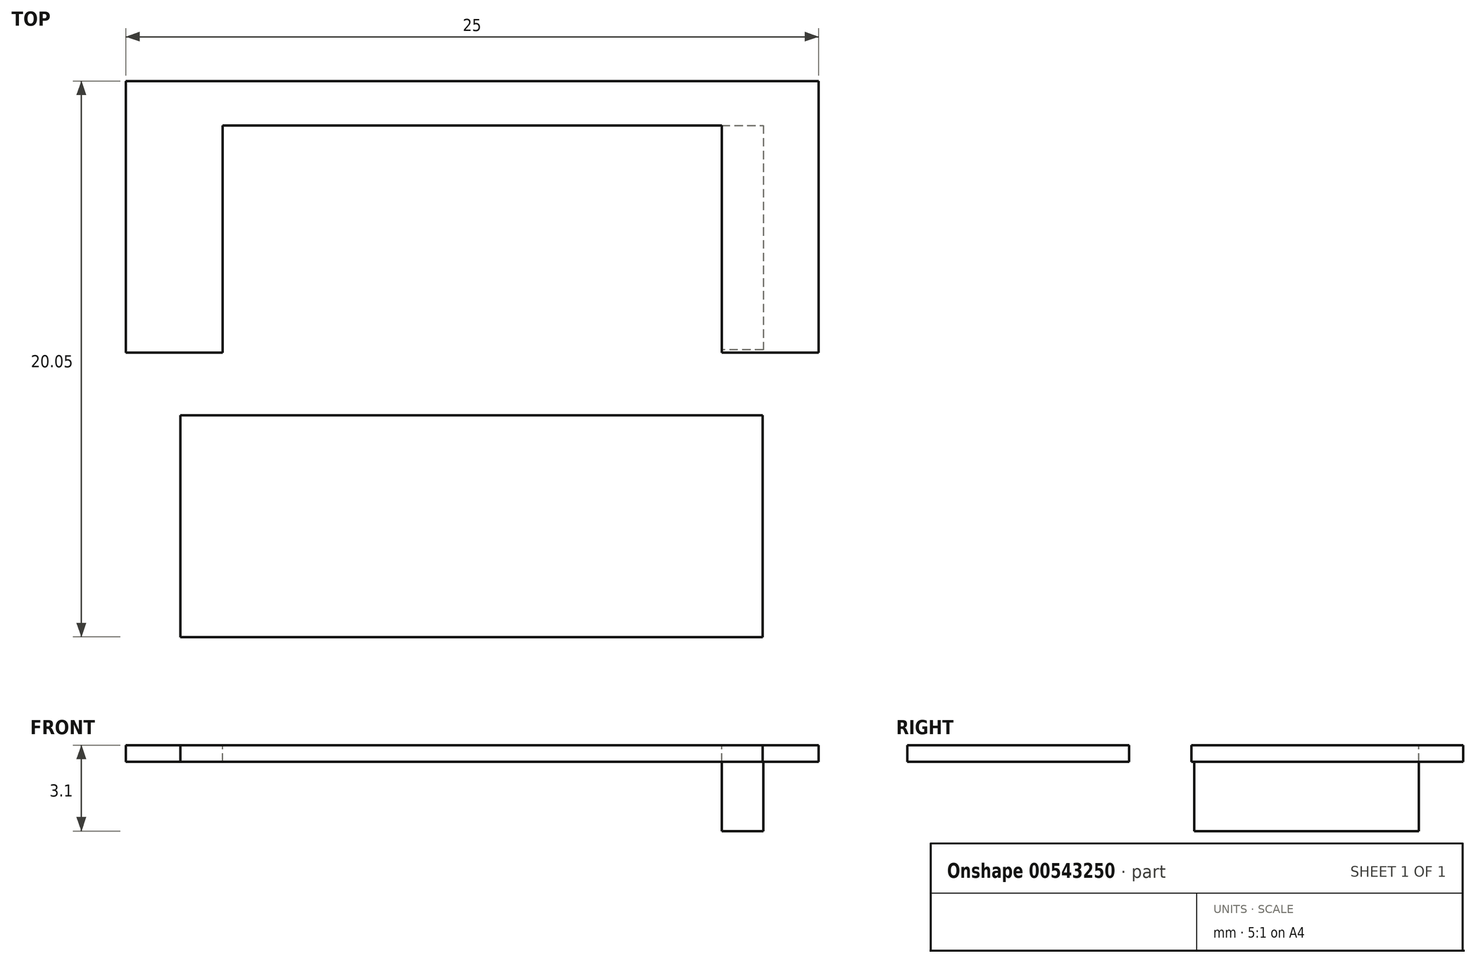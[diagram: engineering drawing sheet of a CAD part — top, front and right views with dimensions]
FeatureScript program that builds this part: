
annotation { "Feature Type Name" : "Feature", "Feature Type Description" : "" }
export const myFeature = defineFeature(function(context is Context, id is Id, definition is map)
    precondition{}
    {
        {
            var Q0;
            Q0=qCreatedBy(makeId("Top.planeOp"),FACE);
            var sketch = newSketch(context, id + "F0", { "sketchPlane" : qUnion([Q0])});
            skLineSegment(sketch, "E0.bottom", {"start": v(-20.52, -0.28) * mm, "end": v(4.48, -0.28) * mm});
            skLineSegment(sketch, "E0.top", {"start": v(-20.52, -10.08) * mm, "end": v(4.48, -10.08) * mm});
            skLineSegment(sketch, "E0.left", {"start": v(-20.52, -0.28) * mm, "end": v(-20.52, -10.08) * mm});
            skLineSegment(sketch, "E0.right", {"start": v(4.48, -0.28) * mm, "end": v(4.48, -10.08) * mm});
            skLineSegment(sketch, "E1.bottom", {"start": v(-17.02, -3.48) * mm, "end": v(0.98, -3.48) * mm});
            skLineSegment(sketch, "E1.top", {"start": v(-17.02, -6.98) * mm, "end": v(0.98, -6.98) * mm});
            skLineSegment(sketch, "E1.left", {"start": v(-17.02, -3.48) * mm, "end": v(-17.02, -6.98) * mm});
            skLineSegment(sketch, "E1.right", {"start": v(0.98, -3.48) * mm, "end": v(0.98, -6.98) * mm});
            skLineSegment(sketch, "E2", {"start": v(-17.02, -6.98) * mm, "end": v(-17.02, -10.08) * mm});
            skLineSegment(sketch, "E3", {"start": v(0.98, -6.98) * mm, "end": v(0.98, -10.08) * mm});
            skLineSegment(sketch, "E4", {"start": v(-17.02, -3.48) * mm, "end": v(-17.02, -0.28) * mm});
            skLineSegment(sketch, "E5", {"start": v(0.98, -3.48) * mm, "end": v(0.98, -0.28) * mm});
            skLineSegment(sketch, "E6", {"start": v(-17.02, -10.08) * mm, "end": v(-18.52, -10.08) * mm});
            skLineSegment(sketch, "E7", {"start": v(-18.52, -10.08) * mm, "end": v(-18.52, -1.88) * mm});
            skLineSegment(sketch, "E8", {"start": v(-18.52, -1.88) * mm, "end": v(2.48, -1.88) * mm});
            skLineSegment(sketch, "E9", {"start": v(2.48, -1.88) * mm, "end": v(2.48, -9.98) * mm});
            skLineSegment(sketch, "E10", {"start": v(2.48, -9.98) * mm, "end": v(0.98, -9.98) * mm});
            skLineSegment(sketch, "E11.bottom", {"start": v(-18.54, -12.33) * mm, "end": v(2.46, -12.33) * mm});
            skLineSegment(sketch, "E11.top", {"start": v(-18.54, -20.33) * mm, "end": v(2.46, -20.33) * mm});
            skLineSegment(sketch, "E11.left", {"start": v(-18.54, -12.33) * mm, "end": v(-18.54, -20.33) * mm});
            skLineSegment(sketch, "E11.right", {"start": v(2.46, -12.33) * mm, "end": v(2.46, -20.33) * mm});
            skCircle(sketch, "E12", {"center": v(-8.02, -5.58) * mm, "radius": 2.85 * mm});
            skPoint(sketch, "E12.centerSnap0", {"position": v(-8.02, -3.48) * mm});
            skSolve(sketch);
        }
        {
            var Q0;
            Q0 = qSketchRegion(id + "F0", true);
            var Q1;
            {var subQ7=sQuery(id+"F0.wireOp",EDGE,"E6");Q1=makeQuery(id+"F0.imprint","IMPRINT",FACE,{"disambiguationData":[TD([[makeQuery(id+"F0.imprint","IMPRINT",EDGE,{"derivedFrom":subQ7}),-1.0]])]});}
            var Q2;
            {var subQ8=sQuery(id+"F0.wireOp",EDGE,"E9");Q2=makeQuery(id+"F0.imprint","IMPRINT",FACE,{"disambiguationData":[TD([[makeQuery(id+"F0.imprint","IMPRINT",EDGE,{"derivedFrom":subQ8}),-1.0]])]});}
            var Q3;
            {var subQ0=sQuery(id+"F0.wireOp",EDGE,"E1.bottom");Q3=makeQuery(id+"F0.imprint","IMPRINT",FACE,{"disambiguationData":[TD([[makeQuery(id+"F0.imprint","IMPRINT",EDGE,{"derivedFrom":subQ0}),1.0]])]});}
            extrude(context, id + "F1", {"entities" : qUnion([Q0, Q1, Q2, Q3]), "depth" : 0.6 * mm, "offsetDistance" : 25 * mm});
        }
        {
            var Q0;
            Q0=makeQuery(id+"F0.imprint","IMPRINT",FACE,{"disambiguationData":[TD([[makeQuery(id+"F0.imprint","IMPRINT",EDGE,{"derivedFrom":sQuery(id+"F0.wireOp",EDGE,"E1.top")}),-1.0]])]});
            extrude(context, id + "F2", {"entities" : qUnion([Q0]), "operationType" : NewBodyOperationType.ADD, "oppositeDirection" : true, "depth" : 4 * mm, "offsetDistance" : 25 * mm});
        }
        {
            var Q0;
            Q0=makeQuery(id+"F2.opExtrude","CAP_EDGE",EDGE,{"disambiguationData":[OSD([sQuery(id+"F0.wireOp",EDGE,"E1.top")])],"isStart":false});
            var Q1;
            Q1=makeQuery(id+"F2.opExtrude","CAP_EDGE",EDGE,{"disambiguationData":[OSD([sQuery(id+"F0.wireOp",EDGE,"E12")])],"isStart":false});
            chamfer(context, id + "F3", {"entities" : qUnion([Q0, Q1]), "width" : 4.6 * mm, "tangentPropagation" : true});
        }
        {
            var Q0;
            Q0=makeQuery(id+"F1.opExtrude","CAP_EDGE",EDGE,{"disambiguationData":[OSD([sQuery(id+"F0.wireOp",EDGE,"E1.bottom")])],"isStart":false});
            chamfer(context, id + "F4", {"entities" : qUnion([Q0]), "width" : 0.6 * mm, "tangentPropagation" : true});
        }
        {
            var Q0;
            {var subQ7=sQuery(id+"F0.wireOp",EDGE,"E6");Q0=makeQuery(id+"F0.imprint","IMPRINT",FACE,{"disambiguationData":[TD([[makeQuery(id+"F0.imprint","IMPRINT",EDGE,{"derivedFrom":subQ7}),-1.0]])]});}
            var Q1;
            {var subQ0=sQuery(id+"F0.wireOp",EDGE,"E1.bottom");Q1=makeQuery(id+"F0.imprint","IMPRINT",FACE,{"disambiguationData":[TD([[makeQuery(id+"F0.imprint","IMPRINT",EDGE,{"derivedFrom":subQ0}),1.0]])]});}
            var Q2;
            {var subQ8=sQuery(id+"F0.wireOp",EDGE,"E9");Q2=makeQuery(id+"F0.imprint","IMPRINT",FACE,{"disambiguationData":[TD([[makeQuery(id+"F0.imprint","IMPRINT",EDGE,{"derivedFrom":subQ8}),-1.0]])]});}
            extrude(context, id + "F5", {"entities" : qUnion([Q0, Q1, Q2]), "operationType" : NewBodyOperationType.ADD, "oppositeDirection" : true, "depth" : 2.5 * mm, "offsetDistance" : 25 * mm});
        }
        {
            var Q0;
            {var subQ0=sQuery(id+"F0.wireOp",EDGE,"E12");var subQ1=sQuery(id+"F0.wireOp",EDGE,"E1.top");var subQ2=makeQuery(id+"F0.imprint","INTERSECT",VERTEX,{"disambiguationData":[OD(0.0)],"derivedFrom":[subQ1,subQ0]});Q0=makeQuery(id+"F0.imprint","IMPRINT",FACE,{"disambiguationData":[TD([[makeQuery(id+"F0.imprint","IMPRINT",EDGE,{"disambiguationData":[TD([[subQ2,-1.0]])],"derivedFrom":subQ1}),-1.0]])]});}
            var Q1;
            {var subQ0=sQuery(id+"F0.wireOp",EDGE,"E12");var subQ1=sQuery(id+"F0.wireOp",EDGE,"E1.bottom");var subQ2=makeQuery(id+"F0.imprint","INTERSECT",VERTEX,{"disambiguationData":[OD(0.0)],"derivedFrom":[subQ1,subQ0]});Q1=makeQuery(id+"F0.imprint","IMPRINT",FACE,{"disambiguationData":[TD([[makeQuery(id+"F0.imprint","IMPRINT",EDGE,{"disambiguationData":[TD([[subQ2,-1.0]])],"derivedFrom":subQ1}),-1.0]])]});}
            var Q2;
            {var subQ0=sQuery(id+"F0.wireOp",EDGE,"E12");var subQ1=sQuery(id+"F0.wireOp",EDGE,"E1.bottom");var subQ2=makeQuery(id+"F0.imprint","INTERSECT",VERTEX,{"disambiguationData":[OD(0.0)],"derivedFrom":[subQ1,subQ0]});Q2=makeQuery(id+"F0.imprint","IMPRINT",FACE,{"disambiguationData":[TD([[makeQuery(id+"F0.imprint","IMPRINT",EDGE,{"disambiguationData":[TD([[subQ2,-1.0]])],"derivedFrom":subQ1}),1.0]])]});}
            extrude(context, id + "F6", {"entities" : qUnion([Q0, Q1, Q2]), "operationType" : NewBodyOperationType.REMOVE, "endBound" : BoundingType.SYMMETRIC, "oppositeDirection" : true, "depth" : 25 * mm, "offsetDistance" : 25 * mm});
        }
    });
